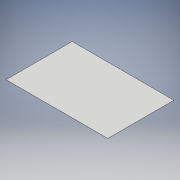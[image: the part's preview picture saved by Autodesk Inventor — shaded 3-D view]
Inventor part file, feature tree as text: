
AUTODESK INVENTOR PART (.ipt)
format: ipt  version: 2017 (Build 210142000, 142)  size: 95,744 bytes
history: native  units: mm
features: sheet_metal_op x1, sketch x1, other x1
ambient origin geometry x8: Origin, YZ Plane, XZ Plane, XY Plane, X Axis, Y Axis, Z Axis, Center Point
bodies: Solid1 (feature_tree)
feature tree (3):
  sheet_metal_op  "Face1"
  sketch  "Sketch1"  dims[d0=400.0mm d1=260.0mm d2=0.5mm]
  other  "Plate1"
